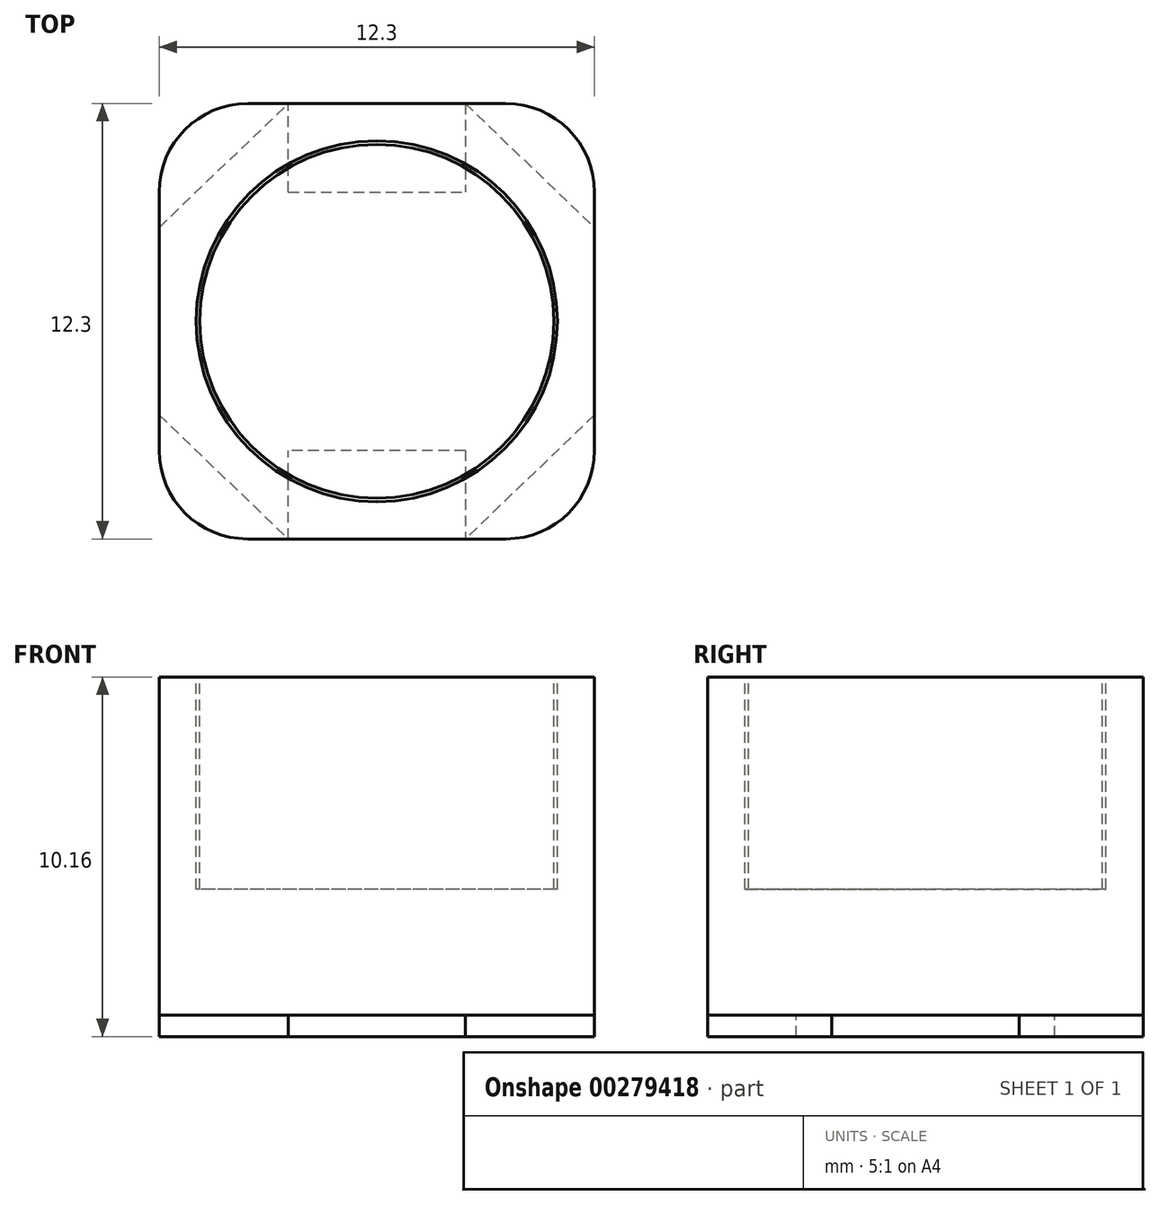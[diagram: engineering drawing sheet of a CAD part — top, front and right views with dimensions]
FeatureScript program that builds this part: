
annotation { "Feature Type Name" : "Feature", "Feature Type Description" : "" }
export const myFeature = defineFeature(function(context is Context, id is Id, definition is map)
    precondition{}
    {
        {
            var Q0;
            Q0=qCreatedBy(makeId("Top.planeOp"),FACE);
            var sketch = newSketch(context, id + "F0", { "sketchPlane" : qUnion([Q0])});
            skLineSegment(sketch, "E0.bottom", {"start": v(3.65, -6.15) * mm, "end": v(-3.65, -6.15) * mm});
            skLineSegment(sketch, "E0.top", {"start": v(3.65, 6.15) * mm, "end": v(-3.65, 6.15) * mm});
            skLineSegment(sketch, "E0.left", {"start": v(6.15, -3.65) * mm, "end": v(6.15, 3.65) * mm});
            skLineSegment(sketch, "E0.right", {"start": v(-6.15, -3.65) * mm, "end": v(-6.15, 3.65) * mm});
            skPoint(sketch, "E0.middle", {"position": v(0, 0) * mm});
            skPoint(sketch, "E1.visualSharp", {"position": v(-6.15, -6.15) * mm});
            skArc(sketch, "E1.filletArc", {"start": v(-6.15, -3.65) * mm, "mid": v(-5.42, -5.42) * mm, "end": v(-3.65, -6.15) * mm});
            skPoint(sketch, "E2.visualSharp", {"position": v(6.15, -6.15) * mm});
            skArc(sketch, "E2.filletArc", {"start": v(3.65, -6.15) * mm, "mid": v(5.42, -5.42) * mm, "end": v(6.15, -3.65) * mm});
            skPoint(sketch, "E3.visualSharp", {"position": v(6.15, 6.15) * mm});
            skArc(sketch, "E3.filletArc", {"start": v(6.15, 3.65) * mm, "mid": v(5.42, 5.42) * mm, "end": v(3.65, 6.15) * mm});
            skPoint(sketch, "E4.visualSharp", {"position": v(-6.15, 6.15) * mm});
            skArc(sketch, "E4.filletArc", {"start": v(-3.65, 6.15) * mm, "mid": v(-5.42, 5.42) * mm, "end": v(-6.15, 3.65) * mm});
            skSolve(sketch);
        }
        {
            var Q0;
            Q0 = qSketchRegion(id + "F0", true);
            extrude(context, id + "F1", {"entities" : qUnion([Q0]), "depth" : 9.56 * mm});
        }
        {
            var Q0;
            Q0=makeQuery(id+"F1.opExtrude","CAP_FACE",FACE,{"disambiguationData":[OSD([sQuery(id+"F0.wireOp",EDGE,"E0.bottom"),sQuery(id+"F0.wireOp",EDGE,"E0.top"),sQuery(id+"F0.wireOp",EDGE,"E0.left"),sQuery(id+"F0.wireOp",EDGE,"E0.right"),sQuery(id+"F0.wireOp",EDGE,"E1.filletArc"),sQuery(id+"F0.wireOp",EDGE,"E2.filletArc"),sQuery(id+"F0.wireOp",EDGE,"E3.filletArc"),sQuery(id+"F0.wireOp",EDGE,"E4.filletArc")])],"isStart":false});
            var sketch = newSketch(context, id + "F2", { "sketchPlane" : qUnion([Q0])});
            skCircle(sketch, "E5", {"center": v(0, 0) * mm, "radius": 4 * mm});
            skSolve(sketch);
        }
        {
            var Q0;
            Q0 = qSketchRegion(id + "F2", true);
            extrude(context, id + "F3", {"entities" : qUnion([Q0]), "operationType" : NewBodyOperationType.ADD, "oppositeDirection" : true, "depth" : 1 * mm});
        }
        {
            var Q0;
            Q0=makeQuery(id+"F1.opExtrude","CAP_FACE",FACE,{"disambiguationData":[OSD([sQuery(id+"F0.wireOp",EDGE,"E0.bottom"),sQuery(id+"F0.wireOp",EDGE,"E0.top"),sQuery(id+"F0.wireOp",EDGE,"E0.left"),sQuery(id+"F0.wireOp",EDGE,"E0.right"),sQuery(id+"F0.wireOp",EDGE,"E1.filletArc"),sQuery(id+"F0.wireOp",EDGE,"E2.filletArc"),sQuery(id+"F0.wireOp",EDGE,"E3.filletArc"),sQuery(id+"F0.wireOp",EDGE,"E4.filletArc")])],"isStart":false});
            var sketch = newSketch(context, id + "F4", { "sketchPlane" : qUnion([Q0])});
            skCircle(sketch, "E6", {"center": v(0, 0) * mm, "radius": 5 * mm});
            skCircle(sketch, "E7", {"center": v(0, 0) * mm, "radius": 5.1 * mm});
            skSolve(sketch);
        }
        {
            var Q0;
            Q0 = qSketchRegion(id + "F4", true);
            extrude(context, id + "F5", {"entities" : qUnion([Q0]), "operationType" : NewBodyOperationType.REMOVE, "oppositeDirection" : true, "depth" : 6 * mm});
        }
        {
            var Q0;
            Q0=makeQuery(id+"F1.opExtrude","CAP_FACE",FACE,{"disambiguationData":[OSD([sQuery(id+"F0.wireOp",EDGE,"E0.bottom"),sQuery(id+"F0.wireOp",EDGE,"E0.top"),sQuery(id+"F0.wireOp",EDGE,"E0.left"),sQuery(id+"F0.wireOp",EDGE,"E0.right"),sQuery(id+"F0.wireOp",EDGE,"E1.filletArc"),sQuery(id+"F0.wireOp",EDGE,"E2.filletArc"),sQuery(id+"F0.wireOp",EDGE,"E3.filletArc"),sQuery(id+"F0.wireOp",EDGE,"E4.filletArc")])],"isStart":true});
            var sketch = newSketch(context, id + "F6", { "sketchPlane" : qUnion([Q0])});
            skLineSegment(sketch, "E8", {"start": v(-6.15, -2.65) * mm, "end": v(-2.5, -6.15) * mm});
            skLineSegment(sketch, "E9", {"start": v(-2.5, -3.65) * mm, "end": v(-2.5, -6.15) * mm});
            skLineSegment(sketch, "E10", {"start": v(-2.5, -3.65) * mm, "end": v(2.5, -3.65) * mm});
            skLineSegment(sketch, "E11", {"start": v(2.5, -6.15) * mm, "end": v(2.5, -3.65) * mm});
            skLineSegment(sketch, "E12", {"start": v(2.5, -6.15) * mm, "end": v(6.15, -2.65) * mm});
            skLineSegment(sketch, "E13", {"start": v(6.15, 2.65) * mm, "end": v(6.15, -2.65) * mm});
            skLineSegment(sketch, "E14", {"start": v(6.15, 2.65) * mm, "end": v(2.5, 6.15) * mm});
            skLineSegment(sketch, "E15", {"start": v(2.5, 3.65) * mm, "end": v(2.5, 6.15) * mm});
            skLineSegment(sketch, "E16", {"start": v(2.5, 3.65) * mm, "end": v(-2.5, 3.65) * mm});
            skLineSegment(sketch, "E17", {"start": v(-2.5, 6.15) * mm, "end": v(-2.5, 3.65) * mm});
            skLineSegment(sketch, "E18", {"start": v(-6.15, -2.65) * mm, "end": v(-6.15, 2.65) * mm});
            skLineSegment(sketch, "E19", {"start": v(-2.5, 3.65) * mm, "end": v(2.5, -3.65) * mm, "construction": true});
            skLineSegment(sketch, "E20", {"start": v(2.5, 3.65) * mm, "end": v(-2.5, -3.65) * mm, "construction": true});
            skLineSegment(sketch, "E21", {"start": v(-2.5, -3.65) * mm, "end": v(-2.5, 3.65) * mm, "construction": true});
            skLineSegment(sketch, "E22", {"start": v(2.5, 3.65) * mm, "end": v(2.5, -3.65) * mm, "construction": true});
            skLineSegment(sketch, "E23", {"start": v(-6.15, 2.65) * mm, "end": v(-2.5, 6.15) * mm});
            skSolve(sketch);
        }
        {
            var Q0;
            Q0 = qSketchRegion(id + "F6", true);
            extrude(context, id + "F7", {"entities" : qUnion([Q0]), "depth" : 0.6 * mm});
        }
        {
            var Q0;
            Q0=makeQuery(id+"F1.opExtrude","CAP_FACE",FACE,{"disambiguationData":[OSD([sQuery(id+"F0.wireOp",EDGE,"E0.bottom"),sQuery(id+"F0.wireOp",EDGE,"E0.top"),sQuery(id+"F0.wireOp",EDGE,"E0.left"),sQuery(id+"F0.wireOp",EDGE,"E0.right"),sQuery(id+"F0.wireOp",EDGE,"E1.filletArc"),sQuery(id+"F0.wireOp",EDGE,"E2.filletArc"),sQuery(id+"F0.wireOp",EDGE,"E3.filletArc"),sQuery(id+"F0.wireOp",EDGE,"E4.filletArc")])],"isStart":true});
            var sketch = newSketch(context, id + "F8", { "sketchPlane" : qUnion([Q0])});
            skLineSegment(sketch, "E24.bottom", {"start": v(-2.5, -6.15) * mm, "end": v(2.5, -6.15) * mm});
            skLineSegment(sketch, "E24.top", {"start": v(-2.5, -3.65) * mm, "end": v(2.5, -3.65) * mm});
            skLineSegment(sketch, "E24.left", {"start": v(-2.5, -3.65) * mm, "end": v(-2.5, -6.15) * mm});
            skLineSegment(sketch, "E24.right", {"start": v(2.5, -3.65) * mm, "end": v(2.5, -6.15) * mm});
            skLineSegment(sketch, "E25.bottom", {"start": v(-2.5, 3.65) * mm, "end": v(2.5, 3.65) * mm});
            skLineSegment(sketch, "E25.top", {"start": v(-2.5, 6.15) * mm, "end": v(2.5, 6.15) * mm});
            skLineSegment(sketch, "E25.left", {"start": v(-2.5, 6.15) * mm, "end": v(-2.5, 3.65) * mm});
            skLineSegment(sketch, "E25.right", {"start": v(2.5, 6.15) * mm, "end": v(2.5, 3.65) * mm});
            skSolve(sketch);
        }
        {
            var Q0;
            Q0 = qSketchRegion(id + "F8", true);
            extrude(context, id + "F9", {"entities" : qUnion([Q0]), "depth" : 0.6 * mm});
        }
    });
